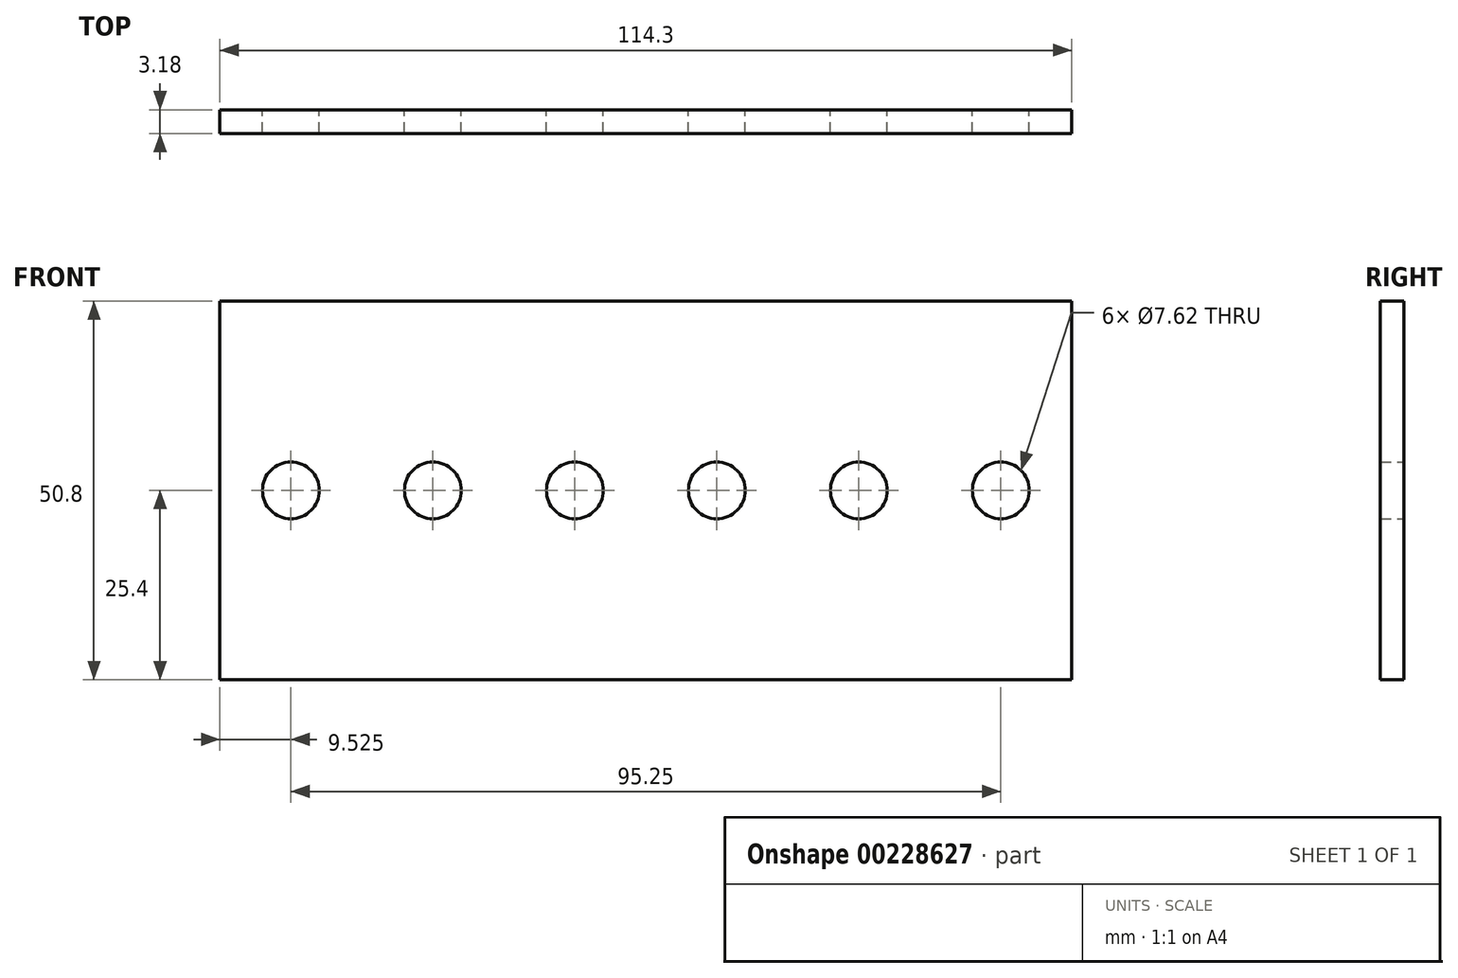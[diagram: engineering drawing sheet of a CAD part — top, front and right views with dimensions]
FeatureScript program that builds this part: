
annotation { "Feature Type Name" : "Feature", "Feature Type Description" : "" }
export const myFeature = defineFeature(function(context is Context, id is Id, definition is map)
    precondition{}
    {
        {
            var Q0;
            Q0=qCreatedBy(makeId("Front.planeOp"),FACE);
            var sketch = newSketch(context, id + "F0", { "sketchPlane" : qUnion([Q0])});
            skLineSegment(sketch, "E0.bottom", {"start": v(57.15, 25.4) * mm, "end": v(-57.15, 25.4) * mm});
            skLineSegment(sketch, "E0.top", {"start": v(57.15, -25.4) * mm, "end": v(-57.15, -25.4) * mm});
            skLineSegment(sketch, "E0.left", {"start": v(57.15, 25.4) * mm, "end": v(57.15, -25.4) * mm});
            skLineSegment(sketch, "E0.right", {"start": v(-57.15, 25.4) * mm, "end": v(-57.15, -25.4) * mm});
            skPoint(sketch, "E0.middle", {"position": v(0, 0) * mm});
            skCircle(sketch, "E1", {"center": v(-9.52, 0) * mm, "radius": 3.81 * mm});
            skCircle(sketch, "E2", {"center": v(-28.57, 0) * mm, "radius": 3.81 * mm});
            skCircle(sketch, "E3", {"center": v(-47.62, 0) * mm, "radius": 3.81 * mm});
            skCircle(sketch, "E4", {"center": v(9.53, 0) * mm, "radius": 3.81 * mm});
            skCircle(sketch, "E5", {"center": v(28.58, 0) * mm, "radius": 3.81 * mm});
            skCircle(sketch, "E6", {"center": v(47.62, 0) * mm, "radius": 3.81 * mm});
            skLineSegment(sketch, "E7", {"start": v(-68.37, 0) * mm, "end": v(69.95, 0) * mm, "construction": true});
            skLineSegment(sketch, "E8", {"start": v(-47.63, 13.9) * mm, "end": v(-47.62, -13.36) * mm, "construction": true});
            skLineSegment(sketch, "E9", {"start": v(-28.57, 13.7) * mm, "end": v(-28.57, -13.55) * mm, "construction": true});
            skLineSegment(sketch, "E10", {"start": v(-9.52, 13.65) * mm, "end": v(-9.52, -13.6) * mm, "construction": true});
            skLineSegment(sketch, "E11", {"start": v(9.53, 13.9) * mm, "end": v(9.53, -13.36) * mm, "construction": true});
            skLineSegment(sketch, "E12", {"start": v(28.58, 13.7) * mm, "end": v(28.58, -13.56) * mm, "construction": true});
            skLineSegment(sketch, "E13", {"start": v(-47.63, 14.08) * mm, "end": v(-47.62, -13.18) * mm, "construction": true});
            skLineSegment(sketch, "E14", {"start": v(47.62, 13.5) * mm, "end": v(47.63, -13.75) * mm, "construction": true});
            skLineSegment(sketch, "E15", {"start": v(0, 13.9) * mm, "end": v(0, -13.35) * mm, "construction": true});
            skSolve(sketch);
        }
        {
            var Q0;
            Q0 = qSketchRegion(id + "F0", true);
            extrude(context, id + "F1", {"entities" : qUnion([Q0]), "depth" : 3.17 * mm});
        }
    });
